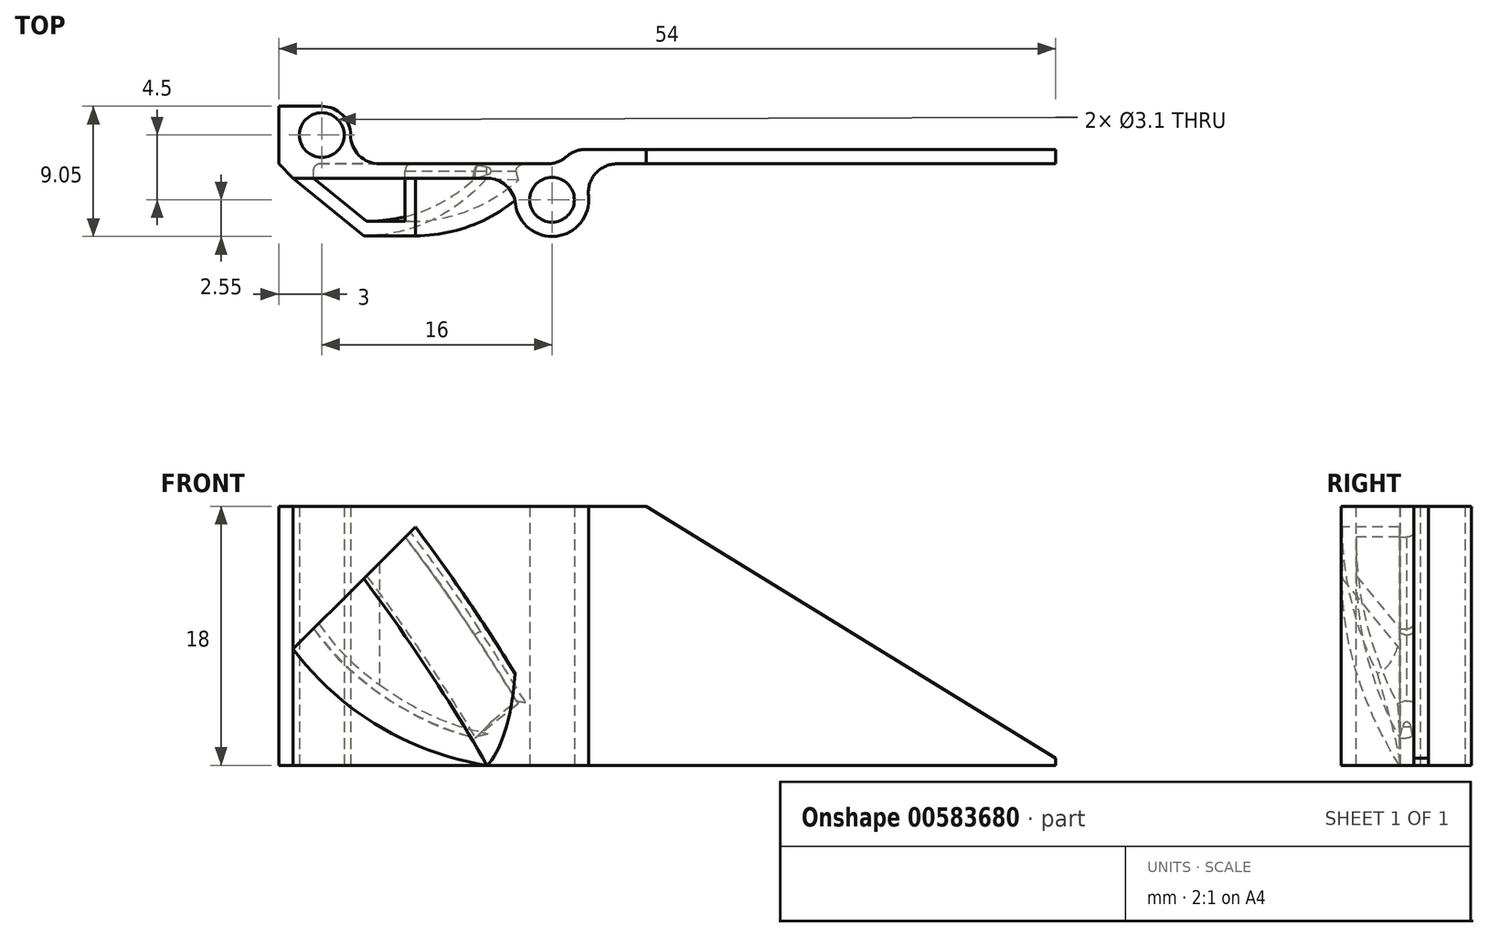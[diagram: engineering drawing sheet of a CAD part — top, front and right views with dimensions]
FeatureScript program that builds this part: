
annotation { "Feature Type Name" : "Feature", "Feature Type Description" : "" }
export const myFeature = defineFeature(function(context is Context, id is Id, definition is map)
    precondition{}
    {
        {
            var Q0;
            Q0=qCreatedBy(makeId("Top.planeOp"),FACE);
            var sketch = newSketch(context, id + "F0", { "sketchPlane" : qUnion([Q0])});
            skLineSegment(sketch, "E0", {"start": v(0, 0) * mm, "end": v(22.1, 0) * mm, "construction": true});
            skLineSegment(sketch, "E1", {"start": v(0, -5) * mm, "end": v(3, -5) * mm});
            skLineSegment(sketch, "E2", {"start": v(0, -5) * mm, "end": v(0, -9) * mm});
            skCircle(sketch, "E3", {"center": v(3, -7) * mm, "radius": 1.55 * mm});
            skCircle(sketch, "E4", {"center": v(19, -11.5) * mm, "radius": 1.55 * mm});
            skLineSegment(sketch, "E5", {"start": v(0, -7) * mm, "end": v(3, -7) * mm, "construction": true});
            skLineSegment(sketch, "E6", {"start": v(0, -9) * mm, "end": v(1, -10) * mm});
            skLineSegment(sketch, "E7", {"start": v(1, -10) * mm, "end": v(14.48, -10) * mm});
            skArc(sketch, "E8", {"start": v(16.47, -11.78) * mm, "mid": v(19.28, -14.03) * mm, "end": v(21.53, -11.22) * mm});
            skPoint(sketch, "E9.visualSharp", {"position": v(16.94, -10) * mm});
            skArc(sketch, "E9.filletArc", {"start": v(16.47, -11.78) * mm, "mid": v(15.81, -10.51) * mm, "end": v(14.48, -10) * mm});
            skArc(sketch, "E10.filletArc", {"start": v(23.52, -9) * mm, "mid": v(22.03, -9.67) * mm, "end": v(21.53, -11.22) * mm});
            skArc(sketch, "E11", {"start": v(3, -5) * mm, "mid": v(4.41, -5.59) * mm, "end": v(5, -7) * mm});
            skArc(sketch, "E12", {"start": v(5, -7) * mm, "mid": v(5.59, -8.41) * mm, "end": v(7, -9) * mm});
            skLineSegment(sketch, "E13", {"start": v(7, -9) * mm, "end": v(18.68, -9) * mm});
            skArc(sketch, "E14", {"start": v(18.68, -9) * mm, "mid": v(19.38, -8.87) * mm, "end": v(20, -8.5) * mm});
            skArc(sketch, "E15", {"start": v(20, -8.5) * mm, "mid": v(20.62, -8.13) * mm, "end": v(21.32, -8) * mm});
            skLineSegment(sketch, "E16", {"start": v(21.32, -8) * mm, "end": v(54, -8) * mm});
            skLineSegment(sketch, "E17", {"start": v(23.52, -9) * mm, "end": v(54, -9) * mm});
            skLineSegment(sketch, "E18", {"start": v(54, -8) * mm, "end": v(54, -9) * mm});
            skSolve(sketch);
        }
        {
            var Q0;
            Q0 = qSketchRegion(id + "F0", true);
            extrude(context, id + "F1", {"entities" : qUnion([Q0]), "depth" : 18 * mm, "offsetDistance" : 25 * mm});
        }
        {
            var Q0;
            Q0=makeQuery(id+"F1.opExtrude","SWEPT_FACE",FACE,{"disambiguationData":[OSD([sQuery(id+"F0.wireOp",EDGE,"E17")])]});
            var sketch = newSketch(context, id + "F2", { "sketchPlane" : qUnion([Q0])});
            skLineSegment(sketch, "E19", {"start": v(25.53, 18) * mm, "end": v(54, 0.5) * mm});
            skLineSegment(sketch, "E20", {"start": v(54, 0.5) * mm, "end": v(54, 18) * mm});
            skLineSegment(sketch, "E21", {"start": v(54, 18) * mm, "end": v(25.53, 18) * mm});
            skSolve(sketch);
        }
        {
            var Q0;
            Q0 = qSketchRegion(id + "F2", true);
            extrude(context, id + "F3", {"entities" : qUnion([Q0]), "operationType" : NewBodyOperationType.REMOVE, "oppositeDirection" : true, "depth" : 25 * mm, "offsetDistance" : 25 * mm});
        }
        {
            var Q0;
            Q0=qCreatedBy(makeId("Right.planeOp"),FACE);
            var Q1;
            Q1=makeQuery(id+"F1.opExtrude","CAP_EDGE",EDGE,{"disambiguationData":[OSD([sQuery(id+"F0.wireOp",EDGE,"E2")])],"isStart":true});
            cPlane(context, id + "F4", {"entities" : qUnion([Q0, Q1]), "cplaneType" : CPlaneType.LINE_ANGLE, "offset" : 25 * mm, "angle" : 45 * degree, "oppositeDirection" : true, "width" : 150 * mm, "height" : 150 * mm});
        }
        {
            var Q0;
            Q0=qCreatedBy(id+"F4.planeOp",FACE);
            cPlane(context, id + "F5", {"entities" : qUnion([Q0]), "cplaneType" : CPlaneType.OFFSET, "offset" : 5 * mm, "width" : 150 * mm, "height" : 150 * mm});
        }
        {
            var Q0;
            Q0=qCreatedBy(id+"F5.planeOp",FACE);
            var sketch = newSketch(context, id + "F6", { "sketchPlane" : qUnion([Q0])});
            skLineSegment(sketch, "E22", {"start": v(10, 17.44) * mm, "end": v(13, 17.44) * mm});
            skLineSegment(sketch, "E23", {"start": v(13, 17.44) * mm, "end": v(13, 13.63) * mm});
            skLineSegment(sketch, "E24", {"start": v(13, 13.63) * mm, "end": v(10, 8.44) * mm});
            skLineSegment(sketch, "E25", {"start": v(10, 17.44) * mm, "end": v(10, 18.44) * mm});
            skLineSegment(sketch, "E26", {"start": v(10, 18.44) * mm, "end": v(14, 18.44) * mm});
            skLineSegment(sketch, "E27", {"start": v(14, 18.44) * mm, "end": v(14, 13.36) * mm});
            skLineSegment(sketch, "E28", {"start": v(14, 13.36) * mm, "end": v(10, 6.44) * mm});
            skLineSegment(sketch, "E29", {"start": v(10, 8.44) * mm, "end": v(10, 6.44) * mm});
            skSolve(sketch);
        }
        {
            var Q0;
            Q0=makeQuery(id+"F1.opExtrude","CAP_VERTEX",VERTEX,{"disambiguationData":[OSD([sQuery(id+"F0.wireOp",EDGE,"E7"),sQuery(id+"F0.wireOp",EDGE,"E9.filletArc")])],"isStart":true});
            var Q1;
            Q1=sQuery(id+"F6.wireOp",VERTEX,"E28.start");
            var Q2;
            Q2=makeQuery(id+"F1.opExtrude","CAP_VERTEX",VERTEX,{"disambiguationData":[OSD([sQuery(id+"F0.wireOp",EDGE,"E6"),sQuery(id+"F0.wireOp",EDGE,"E7")])],"isStart":false});
            cPlane(context, id + "F7", {"entities" : qUnion([Q0, Q1, Q2]), "cplaneType" : CPlaneType.THREE_POINT, "offset" : 0 * mm, "width" : 150 * mm, "height" : 150 * mm});
        }
        {
            var Q0;
            Q0=qCreatedBy(id+"F7.planeOp",FACE);
            var sketch = newSketch(context, id + "F8", { "sketchPlane" : qUnion([Q0])});
            skLineSegment(sketch, "E30", {"start": v(-16.47, 6.85) * mm, "end": v(-16.47, 7.44) * mm, "construction": true});
            skArc(sketch, "E31", {"start": v(-16.47, 6.85) * mm, "mid": v(-15.42, -1.18) * mm, "end": v(-12.36, -8.68) * mm});
            skSolve(sketch);
        }
        {
            var Q0;
            Q0=makeQuery(id+"F6.imprint","IMPRINT",FACE,{"disambiguationData":[TD([[makeQuery(id+"F6.imprint","IMPRINT",EDGE,{"derivedFrom":sQuery(id+"F6.wireOp",EDGE,"E22")}),1.0]])]});
            var Q1;
            Q1=sQuery(id+"F8.wireOp",EDGE,"E31");
            sweep(context, id + "F9", {"operationType" : NewBodyOperationType.ADD, "profiles" : qUnion([Q0]), "path" : qUnion([Q1]), "keepProfileOrientation" : true});
        }
        {
            var Q0;
            {var subQ0=sQuery(id+"F0.wireOp",EDGE,"E13");var subQ1=sQuery(id+"F0.wireOp",EDGE,"E9.filletArc");var subQ4=sQuery(id+"F0.wireOp",EDGE,"E7");var subQ5=sQuery(id+"F0.wireOp",EDGE,"E6");var subQ6=sQuery(id+"F0.wireOp",EDGE,"E11");var subQ7=sQuery(id+"F0.wireOp",EDGE,"E1");var subQ8=sQuery(id+"F0.wireOp",EDGE,"E12");var subQ9=sQuery(id+"F0.wireOp",EDGE,"E3");var subQ10=sQuery(id+"F0.wireOp",EDGE,"E2");var subQ11=makeQuery(id+"F1.opExtrude","CAP_FACE",FACE,{"disambiguationData":[OSD([subQ7,subQ10,subQ9,sQuery(id+"F0.wireOp",EDGE,"E4"),subQ5,subQ4,sQuery(id+"F0.wireOp",EDGE,"E8"),subQ1,sQuery(id+"F0.wireOp",EDGE,"E10.filletArc"),subQ6,subQ8,subQ0,sQuery(id+"F0.wireOp",EDGE,"E14"),sQuery(id+"F0.wireOp",EDGE,"E15"),sQuery(id+"F0.wireOp",EDGE,"E16"),sQuery(id+"F0.wireOp",EDGE,"E17"),sQuery(id+"F0.wireOp",EDGE,"E18")])],"isStart":true});Q0=makeQuery(id+"F9.boolean.opBoolean","SPLIT",FACE,{"disambiguationData":[TD([makeQuery(id+"F1.opExtrude","SWEPT_FACE",FACE,{"disambiguationData":[OSD([subQ7])]})])],"derivedFrom":subQ11});}
            var sketch = newSketch(context, id + "F10", { "sketchPlane" : qUnion([Q0])});
            skArc(sketch, "E32.0", {"start": v(5, 7) * mm, "mid": v(5.59, 8.41) * mm, "end": v(7, 9) * mm});
            skLineSegment(sketch, "E33.0", {"start": v(7, 9) * mm, "end": v(8.8, 9) * mm});
            skLineSegment(sketch, "E34", {"start": v(8.8, 9) * mm, "end": v(18.57, 9) * mm});
            skLineSegment(sketch, "E35", {"start": v(18.57, 9) * mm, "end": v(18.57, 4.55) * mm});
            skLineSegment(sketch, "E36", {"start": v(18.57, 4.55) * mm, "end": v(5, 4.55) * mm});
            skLineSegment(sketch, "E37", {"start": v(5, 4.55) * mm, "end": v(5, 7) * mm});
            skSolve(sketch);
        }
        {
            var Q0;
            Q0 = qSketchRegion(id + "F10", true);
            extrude(context, id + "F11", {"entities" : qUnion([Q0]), "operationType" : NewBodyOperationType.REMOVE, "oppositeDirection" : true, "depth" : 25 * mm, "offsetDistance" : 25 * mm, "hasSecondDirection" : true, "secondDirectionOppositeDirection" : false, "secondDirectionDepth" : 25 * mm});
        }
        {
            var Q0;
            {var subQ0=sQuery(id+"F0.wireOp",EDGE,"E14");var subQ1=sQuery(id+"F8.wireOp",EDGE,"E31");var subQ9=sQuery(id+"F0.wireOp",EDGE,"E13");var subQ24=sQuery(id+"F6.wireOp",EDGE,"E28");var subQ26=makeQuery(id+"F1.opExtrude","SWEPT_FACE",FACE,{"disambiguationData":[OSD([subQ9])]});Q0=makeQuery(id+"F11.boolean.opBoolean","MERGE",FACE,{"derivedFrom":[makeQuery(id+"F9.boolean.opBoolean","SPLIT",FACE,{"disambiguationData":[TD([makeQuery(id+"F9.opSweep","SWEPT_FACE",FACE,{"disambiguationData":[OSD([subQ24,subQ1])]})])],"derivedFrom":subQ26}),makeQuery(id+"F9.boolean.opBoolean","SPLIT",FACE,{"disambiguationData":[TD([makeQuery(id+"F1.opExtrude","SWEPT_FACE",FACE,{"disambiguationData":[OSD([subQ0])]})])],"derivedFrom":subQ26}),makeQuery(id+"F11.opExtrude","SWEPT_FACE",FACE,{"disambiguationData":[OSD([sQuery(id+"F10.wireOp",EDGE,"E33.0"),sQuery(id+"F10.wireOp",EDGE,"E34")])]})]});}
            var sketch = newSketch(context, id + "F12", { "sketchPlane" : qUnion([Q0])});
            skLineSegment(sketch, "E38", {"start": v(-18.68, 0) * mm, "end": v(-7, 0) * mm});
            skLineSegment(sketch, "E39", {"start": v(-7, 0) * mm, "end": v(-7, -2.24) * mm});
            skLineSegment(sketch, "E40", {"start": v(-7, -2.24) * mm, "end": v(-18.68, -2.24) * mm});
            skLineSegment(sketch, "E41", {"start": v(-18.68, -2.24) * mm, "end": v(-18.68, 0) * mm});
            skLineSegment(sketch, "E42", {"start": v(-8.8, 15.86) * mm, "end": v(-2.43, 9.5) * mm});
            skFitSpline(sketch, "E43.0", {"points": [v(-14.48, 7.66) * mm, v(-12.69, 10.46) * mm, v(-10.79, 13.2) * mm, v(-8.8, 15.86) * mm]});
            skFitSpline(sketch, "E44.0", {"points": [v(-14.48, 7.66) * mm, v(-14.7, 7.3) * mm, v(-15.04, 6.76) * mm, v(-15.48, 6.06) * mm, v(-15.69, 5.72) * mm, v(-15.8, 5.55) * mm]});
            skFitSpline(sketch, "E45.0", {"points": [v(-15.8, 5.55) * mm, v(-15.72, 5.3) * mm, v(-15.58, 4.8) * mm, v(-15.31, 4.05) * mm, v(-15.03, 3.46) * mm, v(-14.74, 3) * mm, v(-14.57, 2.8) * mm, v(-14.48, 2.7) * mm]});
            skLineSegment(sketch, "E46.0", {"start": v(-13.67, 1.9) * mm, "end": v(-14.48, 2.7) * mm});
            skFitSpline(sketch, "E47.0", {"points": [v(-2.43, 9.5) * mm, v(-3.12, 8.57) * mm, v(-4.26, 7.28) * mm, v(-5.99, 5.77) * mm, v(-7.39, 4.74) * mm, v(-8.86, 3.83) * mm, v(-10.93, 2.79) * mm, v(-12.56, 2.2) * mm, v(-13.67, 1.9) * mm]});
            skSolve(sketch);
        }
        {
            var Q0;
            Q0 = qSketchRegion(id + "F12", true);
            extrude(context, id + "F13", {"entities" : qUnion([Q0]), "operationType" : NewBodyOperationType.REMOVE, "oppositeDirection" : true, "depth" : 1 * mm, "offsetDistance" : 25 * mm});
        }
        {
            var Q0;
            Q0=makeQuery(id+"F9.opSweep","CAP_FACE",FACE,{"disambiguationData":[OSD([sQuery(id+"F6.wireOp",EDGE,"E22"),sQuery(id+"F6.wireOp",EDGE,"E23"),sQuery(id+"F6.wireOp",EDGE,"E24"),sQuery(id+"F6.wireOp",EDGE,"E25"),sQuery(id+"F6.wireOp",EDGE,"E26"),sQuery(id+"F6.wireOp",EDGE,"E27"),sQuery(id+"F6.wireOp",EDGE,"E28"),sQuery(id+"F6.wireOp",EDGE,"E29"),sQuery(id+"F8.wireOp",VERTEX,"E31.start")])],"isStart":true});
            var sketch = newSketch(context, id + "F14", { "sketchPlane" : qUnion([Q0])});
            skLineSegment(sketch, "E48", {"start": v(10, 17.44) * mm, "end": v(13, 17.44) * mm});
            skLineSegment(sketch, "E49", {"start": v(13, 17.44) * mm, "end": v(13, 13.63) * mm});
            skLineSegment(sketch, "E50", {"start": v(13, 13.63) * mm, "end": v(10, 13.63) * mm});
            skLineSegment(sketch, "E51", {"start": v(10, 13.63) * mm, "end": v(10, 17.44) * mm});
            skSolve(sketch);
        }
        {
            var Q0;
            Q0 = qSketchRegion(id + "F14", true);
            var Q1;
            Q1=makeQuery(id+"F9.opSweep","SWEPT_EDGE",EDGE,{"disambiguationData":[OSD([sQuery(id+"F6.wireOp",EDGE,"E23"),sQuery(id+"F6.wireOp",EDGE,"E24"),sQuery(id+"F8.wireOp",EDGE,"E31")])]});
            sweep(context, id + "F15", {"operationType" : NewBodyOperationType.REMOVE, "profiles" : qUnion([Q0]), "path" : qUnion([Q1])});
        }
        {
            var Q0;
            {var subQ0=sQuery(id+"F8.wireOp",EDGE,"E31");var subQ1=sQuery(id+"F6.wireOp",EDGE,"E24");var subQ2=sQuery(id+"F6.wireOp",EDGE,"E23");var subQ3=sQuery(id+"F0.wireOp",EDGE,"E14");var subQ11=sQuery(id+"F0.wireOp",EDGE,"E13");var subQ25=sQuery(id+"F6.wireOp",EDGE,"E28");var subQ27=makeQuery(id+"F1.opExtrude","SWEPT_FACE",FACE,{"disambiguationData":[OSD([subQ11])]});Q0=makeQuery(id+"F15.boolean.opBoolean","INTERSECT",EDGE,{"derivedFrom":[makeQuery(id+"F11.boolean.opBoolean","MERGE",FACE,{"derivedFrom":[makeQuery(id+"F9.boolean.opBoolean","SPLIT",FACE,{"disambiguationData":[TD([makeQuery(id+"F9.opSweep","SWEPT_FACE",FACE,{"disambiguationData":[OSD([subQ25,subQ0])]})])],"derivedFrom":subQ27}),makeQuery(id+"F9.boolean.opBoolean","SPLIT",FACE,{"disambiguationData":[TD([makeQuery(id+"F1.opExtrude","SWEPT_FACE",FACE,{"disambiguationData":[OSD([subQ3])]})])],"derivedFrom":subQ27}),makeQuery(id+"F11.opExtrude","SWEPT_FACE",FACE,{"disambiguationData":[OSD([sQuery(id+"F10.wireOp",EDGE,"E33.0"),sQuery(id+"F10.wireOp",EDGE,"E34")])]})]}),makeQuery(id+"F15.opSweep","SWEPT_FACE",FACE,{"disambiguationData":[OSD([subQ2,subQ1,subQ0,sQuery(id+"F14.wireOp",EDGE,"E48")])]})]});}
            var Q1;
            {var subQ0=sQuery(id+"F8.wireOp",EDGE,"E31");var subQ1=sQuery(id+"F6.wireOp",EDGE,"E24");var subQ2=sQuery(id+"F6.wireOp",EDGE,"E23");var subQ3=sQuery(id+"F0.wireOp",EDGE,"E7");var subQ4=sQuery(id+"F0.wireOp",EDGE,"E14");var subQ12=sQuery(id+"F0.wireOp",EDGE,"E13");var subQ25=sQuery(id+"F6.wireOp",EDGE,"E28");var subQ27=makeQuery(id+"F1.opExtrude","SWEPT_FACE",FACE,{"disambiguationData":[OSD([subQ12])]});Q1=makeQuery(id+"F15.boolean.opBoolean","INTERSECT",EDGE,{"derivedFrom":[makeQuery(id+"F11.boolean.opBoolean","MERGE",FACE,{"derivedFrom":[makeQuery(id+"F9.boolean.opBoolean","SPLIT",FACE,{"disambiguationData":[TD([makeQuery(id+"F9.opSweep","SWEPT_FACE",FACE,{"disambiguationData":[OSD([subQ25,subQ0])]})])],"derivedFrom":subQ27}),makeQuery(id+"F9.boolean.opBoolean","SPLIT",FACE,{"disambiguationData":[TD([makeQuery(id+"F1.opExtrude","SWEPT_FACE",FACE,{"disambiguationData":[OSD([subQ4])]})])],"derivedFrom":subQ27}),makeQuery(id+"F11.opExtrude","SWEPT_FACE",FACE,{"disambiguationData":[OSD([sQuery(id+"F10.wireOp",EDGE,"E33.0"),sQuery(id+"F10.wireOp",EDGE,"E34")])]})]}),makeQuery(id+"F15.opSweep","CAP_FACE",FACE,{"disambiguationData":[OSD([subQ3,subQ2,subQ1,subQ0,sQuery(id+"F12.wireOp",EDGE,"E46.0"),sQuery(id+"F12.wireOp",EDGE,"E47.0"),sQuery(id+"F14.wireOp",EDGE,"E48"),sQuery(id+"F14.wireOp",EDGE,"E49"),sQuery(id+"F14.wireOp",EDGE,"E50"),sQuery(id+"F14.wireOp",EDGE,"E51")])],"isStart":false})]});}
            var Q2;
            {var subQ0=sQuery(id+"F12.wireOp",EDGE,"E47.0");Q2=makeQuery(id+"F13.boolean.opBoolean","COPY",EDGE,{"disambiguationData":[topologyDisambiguationEdgeConnected([makeQuery(id+"F1.opExtrude","SWEPT_FACE",FACE,{"disambiguationData":[OSD([sQuery(id+"F0.wireOp",EDGE,"E13")])]})])],"derivedFrom":makeQuery(id+"F13.opExtrude","CAP_EDGE",EDGE,{"disambiguationData":[OSD([subQ0])],"isStart":true})});}
            var Q3;
            Q3=makeQuery(id+"F13.boolean.opBoolean","COPY",EDGE,{"derivedFrom":makeQuery(id+"F13.opExtrude","CAP_EDGE",EDGE,{"disambiguationData":[OSD([sQuery(id+"F12.wireOp",EDGE,"E46.0")])],"isStart":true})});
            fillet(context, id + "F16", {"entities" : qUnion([Q0, Q1, Q2, Q3]), "radius" : .5 * mm, "tangentPropagation" : true, "allowEdgeOverflow" : false});
        }
    });
